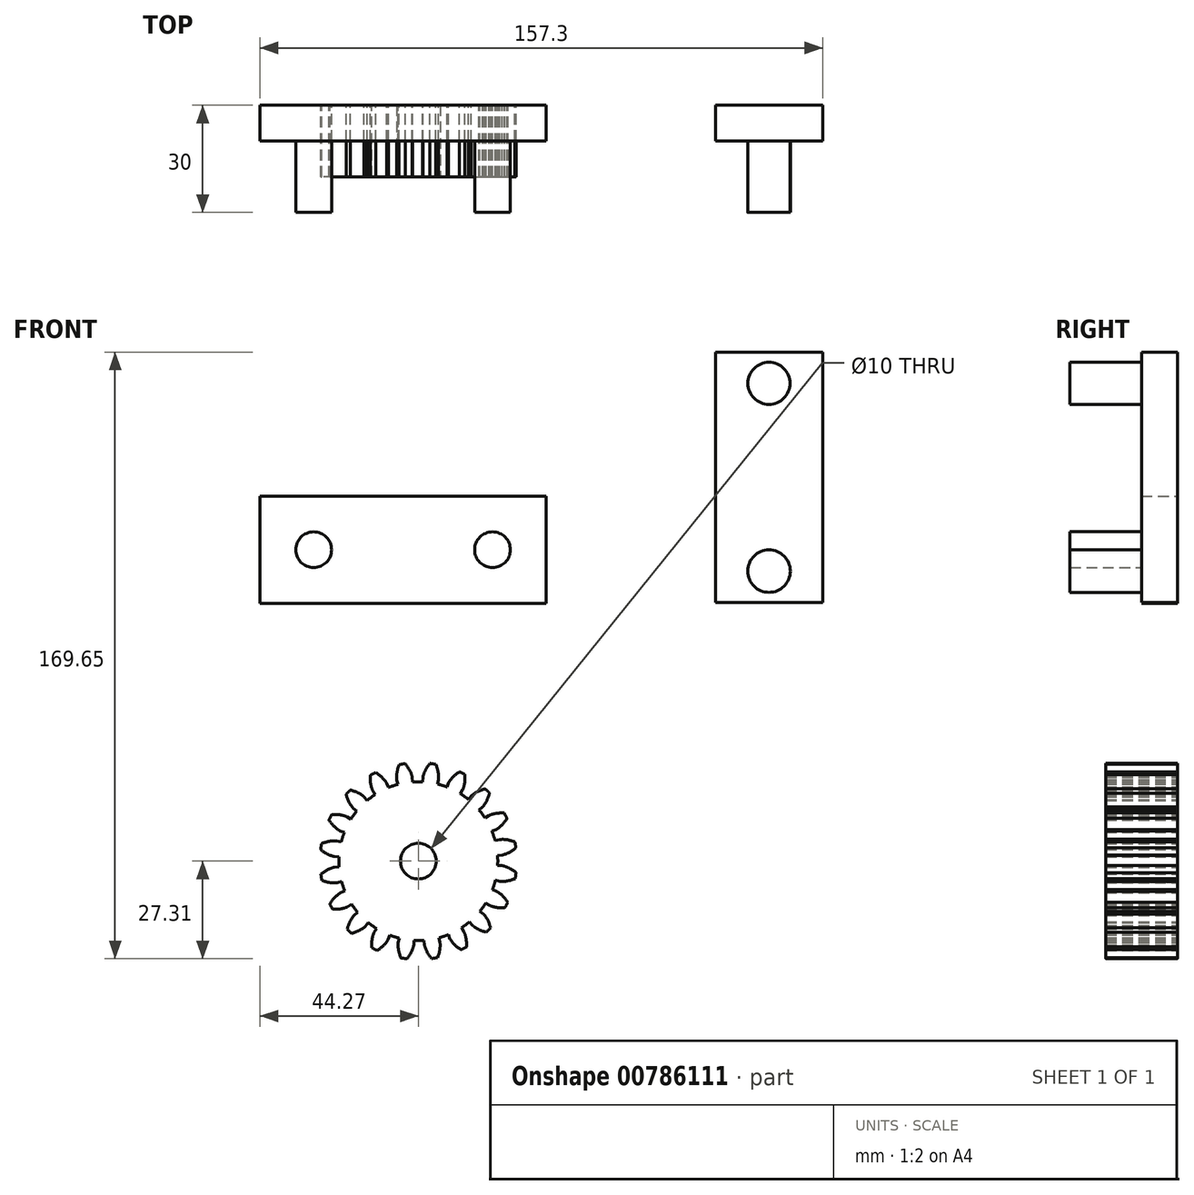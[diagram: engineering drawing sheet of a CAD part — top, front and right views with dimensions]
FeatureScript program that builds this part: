
annotation { "Feature Type Name" : "Feature", "Feature Type Description" : "" }
export const myFeature = defineFeature(function(context is Context, id is Id, definition is map)
    precondition{}
    {
        {
            var Q0;
            Q0=qCreatedBy(makeId("Front.planeOp"),FACE);
            var sketch = newSketch(context, id + "F0", { "sketchPlane" : qUnion([Q0])});
            skArc(sketch, "E0.0", {"start": v(-3.7, 27.25) * mm, "mid": v(-4.55, 27.12) * mm, "end": v(-5.4, 26.97) * mm});
            skFitSpline(sketch, "E1", {"points": [v(-6.03, 22.7) * mm, v(-6.06, 22.88) * mm, v(-6.08, 23.4) * mm, v(-6.05, 24.27) * mm, v(-5.85, 25.47) * mm, v(-5.4, 26.97) * mm], "startDerivative": vector(-0.34, 1.58) * mm, "endDerivative": vector(1.75, 5.4) * mm});
            skCircle(sketch, "E2", {"center": v(-120, 0) * mm, "radius": 25 * mm});
            skCircle(sketch, "E3.0", {"center": v(-120, 0) * mm, "radius": 27.5 * mm});
            skCircle(sketch, "E4.0", {"center": v(-120, 0) * mm, "radius": 22.2 * mm});
            skLineSegment(sketch, "E5", {"start": v(-140.88, 25) * mm, "end": v(-101.92, 25) * mm, "construction": true});
            skLineSegment(sketch, "E6", {"start": v(-111.97, 22.08) * mm, "end": v(-125.4, 26.97) * mm});
            skArc(sketch, "E7", {"start": v(-111.97, 22.08) * mm, "mid": v(-118.95, 23.47) * mm, "end": v(-126.03, 22.7) * mm});
            skLineSegment(sketch, "E8", {"start": v(-125.4, 26.97) * mm, "end": v(-120, 0) * mm});
            skLineSegment(sketch, "E9", {"start": v(-111.97, 22.08) * mm, "end": v(-120, 0) * mm});
            skLineSegment(sketch, "E10", {"start": v(-126.03, 22.7) * mm, "end": v(-120, 0) * mm});
            skPoint(sketch, "E11", {"position": v(-111.97, 22.08) * mm});
            skPoint(sketch, "E12", {"position": v(-114.7, 22.89) * mm});
            skPoint(sketch, "E13", {"position": v(-117.52, 23.36) * mm});
            skPoint(sketch, "E14", {"position": v(-120.36, 22.2) * mm});
            skPoint(sketch, "E15", {"position": v(-123.23, 23.27) * mm});
            skLineSegment(sketch, "E16", {"start": v(-117.52, 23.36) * mm, "end": v(-120, 0) * mm});
            skLineSegment(sketch, "E17", {"start": v(-120.36, 22.2) * mm, "end": v(-120, 0) * mm});
            skLineSegment(sketch, "E18", {"start": v(-123.23, 23.27) * mm, "end": v(-120, 0) * mm});
            skLineSegment(sketch, "E19", {"start": v(-114.7, 22.89) * mm, "end": v(-120, 0) * mm});
            skLineSegment(sketch, "E20", {"start": v(-120.36, 22.2) * mm, "end": v(-120.36, 23.49) * mm});
            skLineSegment(sketch, "E21", {"start": v(-114.7, 22.89) * mm, "end": v(-125.85, 25.47) * mm});
            skLineSegment(sketch, "E22", {"start": v(-117.52, 23.36) * mm, "end": v(-126.05, 24.27) * mm});
            skLineSegment(sketch, "E23", {"start": v(-120.36, 23.49) * mm, "end": v(-126.08, 23.4) * mm});
            skLineSegment(sketch, "E24", {"start": v(-123.23, 23.27) * mm, "end": v(-126.06, 22.88) * mm});
            skFitSpline(sketch, "E25", {"points": [v(-126.03, 22.7) * mm, v(-126.06, 22.88) * mm, v(-126.08, 23.4) * mm, v(-126.05, 24.27) * mm, v(-125.85, 25.47) * mm, v(-125.4, 26.97) * mm], "startDerivative": vector(-0.34, 1.58) * mm, "endDerivative": vector(1.75, 5.4) * mm});
            skFitSpline(sketch, "E26.MirrorCS", {"points": [v(-1.7, 23.43) * mm, v(-1.73, 23.6) * mm, v(-1.89, 24.1) * mm, v(-2.19, 24.91) * mm, v(-2.78, 25.98) * mm, v(-3.7, 27.25) * mm], "startDerivative": vector(-0.2, 1.6) * mm, "endDerivative": vector(-3.42, 4.53) * mm});
            skLineSegment(sketch, "E27.MirrorCS", {"start": v(-1.7, 23.43) * mm, "end": v(-1.6, 22.14) * mm});
            skCircle(sketch, "E28", {"center": v(101.91, -1.04) * mm, "radius": 25 * mm});
            skCircle(sketch, "E29.0", {"center": v(101.91, -1.04) * mm, "radius": 27.5 * mm});
            skCircle(sketch, "E30.0", {"center": v(101.91, -1.04) * mm, "radius": 22.2 * mm});
            skLineSegment(sketch, "E31", {"start": v(95.88, 21.66) * mm, "end": v(101.91, -1.04) * mm});
            skFitSpline(sketch, "E32", {"points": [v(95.88, 21.66) * mm, v(95.85, 21.84) * mm, v(95.84, 22.36) * mm, v(95.86, 23.23) * mm, v(96.07, 24.43) * mm, v(96.52, 25.93) * mm], "startDerivative": vector(-0.34, 1.58) * mm, "endDerivative": vector(1.75, 5.4) * mm});
            skLineSegment(sketch, "E33", {"start": v(101.91, -1.04) * mm, "end": v(95.86, 23.22) * mm});
            skLineSegment(sketch, "E34.1.0", {"start": v(101.91, -1.02) * mm, "end": v(92.14, 21.99) * mm});
            skLineSegment(sketch, "E34.2.0", {"start": v(101.9, -1) * mm, "end": v(88.65, 20.2) * mm});
            skLineSegment(sketch, "E34.3.0", {"start": v(101.9, -0.99) * mm, "end": v(85.49, 17.87) * mm});
            skLineSegment(sketch, "E34.4.0", {"start": v(101.88, -0.98) * mm, "end": v(82.73, 15.09) * mm});
            skLineSegment(sketch, "E34.5.0", {"start": v(101.87, -0.96) * mm, "end": v(80.43, 11.9) * mm});
            skLineSegment(sketch, "E34.6.0", {"start": v(101.85, -0.95) * mm, "end": v(78.67, 8.4) * mm});
            skLineSegment(sketch, "E34.7.0", {"start": v(101.83, -0.95) * mm, "end": v(77.47, 4.67) * mm});
            skLineSegment(sketch, "E34.8.0", {"start": v(101.82, -0.94) * mm, "end": v(76.88, 0.8) * mm});
            skLineSegment(sketch, "E34.9.0", {"start": v(101.8, -0.94) * mm, "end": v(76.9, -3.13) * mm});
            skLineSegment(sketch, "E34.10.0", {"start": v(101.78, -0.94) * mm, "end": v(77.52, -7) * mm});
            skLineSegment(sketch, "E34.11.0", {"start": v(101.76, -0.95) * mm, "end": v(78.75, -10.72) * mm});
            skLineSegment(sketch, "E34.12.0", {"start": v(101.74, -0.95) * mm, "end": v(80.55, -14.2) * mm});
            skLineSegment(sketch, "E34.13.0", {"start": v(101.73, -0.96) * mm, "end": v(82.86, -17.37) * mm});
            skLineSegment(sketch, "E34.14.0", {"start": v(101.71, -0.98) * mm, "end": v(85.65, -20.13) * mm});
            skLineSegment(sketch, "E34.15.0", {"start": v(101.7, -1) * mm, "end": v(88.83, -22.42) * mm});
            skLineSegment(sketch, "E34.16.0", {"start": v(101.7, -1) * mm, "end": v(92.33, -24.19) * mm});
            skLineSegment(sketch, "E34.17.0", {"start": v(101.69, -1.02) * mm, "end": v(96.07, -25.38) * mm});
            skLineSegment(sketch, "E34.18.0", {"start": v(101.68, -1.04) * mm, "end": v(99.94, -25.98) * mm});
            skLineSegment(sketch, "E34.19.0", {"start": v(101.68, -1.06) * mm, "end": v(103.87, -25.96) * mm});
            skLineSegment(sketch, "E34.20.0", {"start": v(101.68, -1.08) * mm, "end": v(107.74, -25.33) * mm});
            skLineSegment(sketch, "E34.21.0", {"start": v(101.69, -1.1) * mm, "end": v(111.46, -24.1) * mm});
            skLineSegment(sketch, "E34.22.0", {"start": v(101.7, -1.11) * mm, "end": v(114.95, -22.31) * mm});
            skLineSegment(sketch, "E34.23.0", {"start": v(101.7, -1.13) * mm, "end": v(118.1, -20) * mm});
            skLineSegment(sketch, "E34.24.0", {"start": v(101.72, -1.14) * mm, "end": v(120.87, -17.2) * mm});
            skLineSegment(sketch, "E34.25.0", {"start": v(101.73, -1.16) * mm, "end": v(123.16, -14.03) * mm});
            skLineSegment(sketch, "E34.26.0", {"start": v(101.75, -1.17) * mm, "end": v(124.93, -10.52) * mm});
            skLineSegment(sketch, "E34.27.0", {"start": v(101.76, -1.17) * mm, "end": v(126.12, -6.79) * mm});
            skLineSegment(sketch, "E34.28.0", {"start": v(101.78, -1.18) * mm, "end": v(126.72, -2.91) * mm});
            skLineSegment(sketch, "E34.29.0", {"start": v(101.8, -1.18) * mm, "end": v(126.7, 1) * mm});
            skLineSegment(sketch, "E34.30.0", {"start": v(101.82, -1.18) * mm, "end": v(126.07, 4.88) * mm});
            skLineSegment(sketch, "E34.31.0", {"start": v(101.84, -1.17) * mm, "end": v(124.85, 8.6) * mm});
            skLineSegment(sketch, "E34.32.0", {"start": v(101.85, -1.16) * mm, "end": v(123.05, 12.09) * mm});
            skLineSegment(sketch, "E34.33.0", {"start": v(101.87, -1.15) * mm, "end": v(120.73, 15.25) * mm});
            skLineSegment(sketch, "E34.34.0", {"start": v(101.88, -1.14) * mm, "end": v(117.95, 18.01) * mm});
            skLineSegment(sketch, "E34.35.0", {"start": v(101.9, -1.13) * mm, "end": v(114.76, 20.3) * mm});
            skLineSegment(sketch, "E34.36.0", {"start": v(101.9, -1.11) * mm, "end": v(111.26, 22.07) * mm});
            skLineSegment(sketch, "E34.37.0", {"start": v(101.91, -1.1) * mm, "end": v(107.53, 23.27) * mm});
            skLineSegment(sketch, "E34.38.0", {"start": v(101.92, -1.08) * mm, "end": v(103.65, 23.86) * mm});
            skLineSegment(sketch, "E34.39.0", {"start": v(101.92, -1.06) * mm, "end": v(99.73, 23.85) * mm});
            skPoint(sketch, "E34.center", {"position": v(101.8, -1.06) * mm});
            skLineSegment(sketch, "E35", {"start": v(101.91, -1.04) * mm, "end": v(96.33, 32.27) * mm});
            skFitSpline(sketch, "E36.MirrorCS", {"points": [v(100.21, 22.4) * mm, v(100.19, 22.56) * mm, v(100.03, 23.06) * mm, v(99.72, 23.87) * mm, v(99.14, 24.94) * mm, v(98.22, 26.21) * mm], "startDerivative": vector(-0.2, 1.6) * mm, "endDerivative": vector(-3.42, 4.53) * mm});
            skLineSegment(sketch, "E37.MirrorCS", {"start": v(100.21, 22.4) * mm, "end": v(101.91, -1.04) * mm});
            skLineSegment(sketch, "E38", {"start": v(101.91, -1.04) * mm, "end": v(91.07, 29.73) * mm});
            skLineSegment(sketch, "E39.MirrorCS", {"start": v(101.91, -1.04) * mm, "end": v(102.13, 31.59) * mm});
            skLineSegment(sketch, "E40", {"start": v(-6.03, 22.7) * mm, "end": v(-5.7, 21.46) * mm});
            skArc(sketch, "E41", {"start": v(-1.6, 22.14) * mm, "mid": v(-3.67, 21.9) * mm, "end": v(-5.7, 21.46) * mm});
            skSolve(sketch);
        }
        {
            var Q0;
            Q0=makeQuery(id+"F0.imprint","IMPRINT",FACE,{"disambiguationData":[TD([[makeQuery(id+"F0.imprint","IMPRINT",EDGE,{"derivedFrom":sQuery(id+"F0.wireOp",EDGE,"E0.0")}),1.0]])]});
            extrude(context, id + "F1", {"entities" : qUnion([Q0]), "depth" : 20 * mm, "offsetDistance" : 25 * mm});
        }
        {
            var Q0;
            Q0=qCreatedBy(makeId("Top.planeOp"),FACE);
            var sketch = newSketch(context, id + "F2", { "sketchPlane" : qUnion([Q0])});
            skLineSegment(sketch, "E42", {"start": v(0, -28.63) * mm, "end": v(0, 36.77) * mm, "construction": true});
            skSolve(sketch);
        }
        {
            var Q0;
            Q0=makeQuery(id+"F1.opExtrude","SWEPT_BODY",BODY,{"disambiguationData":[OSD([sQuery(id+"F0.wireOp",EDGE,"E0.0"),sQuery(id+"F0.wireOp",EDGE,"E1"),sQuery(id+"F0.wireOp",EDGE,"E26.MirrorCS"),sQuery(id+"F0.wireOp",EDGE,"E27.MirrorCS"),sQuery(id+"F0.wireOp",EDGE,"E40"),sQuery(id+"F0.wireOp",EDGE,"E41")])]});
            var Q1;
            Q1=sQuery(id+"F2.wireOp",EDGE,"E42");
            circularPattern(context, id + "F3", {"entities" : qUnion([Q0]), "axis" : qUnion([Q1]), "angle" : 360 * degree, "instanceCount" : 20, "equalSpace" : true});
        }
        {
            var Q0;
            Q0=qCreatedBy(makeId("Front.planeOp"),FACE);
            var sketch = newSketch(context, id + "F4", { "sketchPlane" : qUnion([Q0])});
            skArc(sketch, "E43", {"start": v(-4.6, 21.72) * mm, "mid": v(3.61, -21.9) * mm, "end": v(-2.62, 22.05) * mm});
            skLineSegment(sketch, "E44", {"start": v(-2.62, 22.05) * mm, "end": v(-3.88, 23.51) * mm});
            skLineSegment(sketch, "E45", {"start": v(-3.88, 23.51) * mm, "end": v(-4.6, 21.72) * mm});
            skLineSegment(sketch, "E46.1.0", {"start": v(-9.3, 20.16) * mm, "end": v(-10.95, 21.16) * mm});
            skLineSegment(sketch, "E46.1.1", {"start": v(-10.95, 21.16) * mm, "end": v(-11.09, 19.23) * mm});
            skLineSegment(sketch, "E46.2.0", {"start": v(-15.08, 16.3) * mm, "end": v(-16.96, 16.74) * mm});
            skLineSegment(sketch, "E46.2.1", {"start": v(-16.96, 16.74) * mm, "end": v(-16.49, 14.87) * mm});
            skLineSegment(sketch, "E46.3.0", {"start": v(-19.37, 10.84) * mm, "end": v(-21.3, 10.68) * mm});
            skLineSegment(sketch, "E46.3.1", {"start": v(-21.3, 10.68) * mm, "end": v(-20.27, 9.04) * mm});
            skLineSegment(sketch, "E46.4.0", {"start": v(-21.78, 4.32) * mm, "end": v(-23.56, 3.58) * mm});
            skLineSegment(sketch, "E46.4.1", {"start": v(-23.56, 3.58) * mm, "end": v(-22.08, 2.34) * mm});
            skLineSegment(sketch, "E46.5.0", {"start": v(-22.05, -2.62) * mm, "end": v(-23.51, -3.88) * mm});
            skLineSegment(sketch, "E46.5.1", {"start": v(-23.51, -3.88) * mm, "end": v(-21.72, -4.6) * mm});
            skLineSegment(sketch, "E46.6.0", {"start": v(-20.16, -9.3) * mm, "end": v(-21.16, -10.95) * mm});
            skLineSegment(sketch, "E46.6.1", {"start": v(-21.16, -10.95) * mm, "end": v(-19.23, -11.09) * mm});
            skLineSegment(sketch, "E46.7.0", {"start": v(-16.3, -15.08) * mm, "end": v(-16.74, -16.96) * mm});
            skLineSegment(sketch, "E46.7.1", {"start": v(-16.74, -16.96) * mm, "end": v(-14.87, -16.49) * mm});
            skLineSegment(sketch, "E46.8.0", {"start": v(-10.84, -19.37) * mm, "end": v(-10.68, -21.3) * mm});
            skLineSegment(sketch, "E46.8.1", {"start": v(-10.68, -21.3) * mm, "end": v(-9.04, -20.27) * mm});
            skLineSegment(sketch, "E46.9.0", {"start": v(-4.32, -21.78) * mm, "end": v(-3.58, -23.56) * mm});
            skLineSegment(sketch, "E46.9.1", {"start": v(-3.58, -23.56) * mm, "end": v(-2.34, -22.08) * mm});
            skLineSegment(sketch, "E46.10.0", {"start": v(2.62, -22.05) * mm, "end": v(3.88, -23.51) * mm});
            skLineSegment(sketch, "E46.10.1", {"start": v(3.88, -23.51) * mm, "end": v(4.6, -21.72) * mm});
            skLineSegment(sketch, "E46.11.0", {"start": v(9.3, -20.16) * mm, "end": v(10.95, -21.16) * mm});
            skLineSegment(sketch, "E46.11.1", {"start": v(10.95, -21.16) * mm, "end": v(11.09, -19.23) * mm});
            skLineSegment(sketch, "E46.12.0", {"start": v(15.08, -16.3) * mm, "end": v(16.96, -16.74) * mm});
            skLineSegment(sketch, "E46.12.1", {"start": v(16.96, -16.74) * mm, "end": v(16.49, -14.87) * mm});
            skLineSegment(sketch, "E46.13.0", {"start": v(19.37, -10.84) * mm, "end": v(21.3, -10.68) * mm});
            skLineSegment(sketch, "E46.13.1", {"start": v(21.3, -10.68) * mm, "end": v(20.27, -9.04) * mm});
            skLineSegment(sketch, "E46.14.0", {"start": v(21.78, -4.32) * mm, "end": v(23.56, -3.58) * mm});
            skLineSegment(sketch, "E46.14.1", {"start": v(23.56, -3.58) * mm, "end": v(22.08, -2.34) * mm});
            skLineSegment(sketch, "E46.15.0", {"start": v(22.05, 2.62) * mm, "end": v(23.51, 3.88) * mm});
            skLineSegment(sketch, "E46.15.1", {"start": v(23.51, 3.88) * mm, "end": v(21.72, 4.6) * mm});
            skLineSegment(sketch, "E46.16.0", {"start": v(20.16, 9.3) * mm, "end": v(21.16, 10.95) * mm});
            skLineSegment(sketch, "E46.16.1", {"start": v(21.16, 10.95) * mm, "end": v(19.23, 11.09) * mm});
            skLineSegment(sketch, "E46.17.0", {"start": v(16.3, 15.08) * mm, "end": v(16.74, 16.96) * mm});
            skLineSegment(sketch, "E46.17.1", {"start": v(16.74, 16.96) * mm, "end": v(14.87, 16.49) * mm});
            skLineSegment(sketch, "E46.18.0", {"start": v(10.84, 19.37) * mm, "end": v(10.68, 21.3) * mm});
            skLineSegment(sketch, "E46.18.1", {"start": v(10.68, 21.3) * mm, "end": v(9.04, 20.27) * mm});
            skLineSegment(sketch, "E46.19.0", {"start": v(4.32, 21.78) * mm, "end": v(3.58, 23.56) * mm});
            skLineSegment(sketch, "E46.19.1", {"start": v(3.58, 23.56) * mm, "end": v(2.34, 22.08) * mm});
            skCircle(sketch, "E47", {"center": v(0, 0) * mm, "radius": 5 * mm});
            skSolve(sketch);
        }
        {
            var Q0;
            Q0=makeQuery(id+"F4.imprint","IMPRINT",FACE,{"disambiguationData":[TD([[makeQuery(id+"F4.imprint","IMPRINT",EDGE,{"derivedFrom":sQuery(id+"F4.wireOp",EDGE,"E43")}),1.0]])]});
            extrude(context, id + "F5", {"entities" : qUnion([Q0]), "operationType" : NewBodyOperationType.ADD, "depth" : 20 * mm, "offsetDistance" : 25 * mm});
        }
        {
            var Q0;
            Q0=qCreatedBy(makeId("Front.planeOp"),FACE);
            var sketch = newSketch(context, id + "F6", { "sketchPlane" : qUnion([Q0])});
            skLineSegment(sketch, "E48.bottom", {"start": v(-44.27, 102.06) * mm, "end": v(35.73, 102.06) * mm});
            skLineSegment(sketch, "E48.top", {"start": v(-44.27, 72.06) * mm, "end": v(35.73, 72.06) * mm});
            skLineSegment(sketch, "E48.left", {"start": v(-44.27, 102.06) * mm, "end": v(-44.27, 72.06) * mm});
            skLineSegment(sketch, "E48.right", {"start": v(35.73, 102.06) * mm, "end": v(35.73, 72.06) * mm});
            skCircle(sketch, "E49", {"center": v(-29.27, 87.06) * mm, "radius": 5 * mm});
            skCircle(sketch, "E50", {"center": v(20.73, 87.06) * mm, "radius": 5 * mm});
            skLineSegment(sketch, "E51", {"start": v(-29.27, 87.06) * mm, "end": v(20.73, 87.06) * mm, "construction": true});
            skSolve(sketch);
        }
        {
            var Q0;
            Q0 = qSketchRegion(id + "F6", true);
            var Q1;
            Q1=makeQuery(id+"F6.imprint","IMPRINT",FACE,{"disambiguationData":[TD([[makeQuery(id+"F6.imprint","IMPRINT",EDGE,{"derivedFrom":sQuery(id+"F6.wireOp",EDGE,"E49")}),1.0]])]});
            var Q2;
            Q2=makeQuery(id+"F6.imprint","IMPRINT",FACE,{"disambiguationData":[TD([[makeQuery(id+"F6.imprint","IMPRINT",EDGE,{"derivedFrom":sQuery(id+"F6.wireOp",EDGE,"E50")}),1.0]])]});
            extrude(context, id + "F7", {"entities" : qUnion([Q0, Q1, Q2]), "depth" : 10 * mm, "offsetDistance" : 25 * mm});
        }
        {
            var Q0;
            Q0=makeQuery(id+"F6.imprint","IMPRINT",FACE,{"disambiguationData":[TD([[makeQuery(id+"F6.imprint","IMPRINT",EDGE,{"derivedFrom":sQuery(id+"F6.wireOp",EDGE,"E49")}),1.0]])]});
            var Q1;
            Q1=makeQuery(id+"F6.imprint","IMPRINT",FACE,{"disambiguationData":[TD([[makeQuery(id+"F6.imprint","IMPRINT",EDGE,{"derivedFrom":sQuery(id+"F6.wireOp",EDGE,"E50")}),1.0]])]});
            extrude(context, id + "F8", {"entities" : qUnion([Q0, Q1]), "operationType" : NewBodyOperationType.ADD, "depth" : 30 * mm, "offsetDistance" : 25 * mm});
        }
        {
            var Q0;
            Q0=qCreatedBy(makeId("Front.planeOp"),FACE);
            var sketch = newSketch(context, id + "F9", { "sketchPlane" : qUnion([Q0])});
            skLineSegment(sketch, "E52.bottom", {"start": v(83.03, 142.34) * mm, "end": v(113.03, 142.34) * mm});
            skLineSegment(sketch, "E52.top", {"start": v(83.03, 72.34) * mm, "end": v(113.03, 72.34) * mm});
            skLineSegment(sketch, "E52.left", {"start": v(83.03, 142.34) * mm, "end": v(83.03, 72.34) * mm});
            skLineSegment(sketch, "E52.right", {"start": v(113.03, 142.34) * mm, "end": v(113.03, 72.34) * mm});
            skCircle(sketch, "E53", {"center": v(98.03, 133.59) * mm, "radius": 5.9 * mm});
            skCircle(sketch, "E54", {"center": v(98.03, 81.09) * mm, "radius": 5.95 * mm});
            skLineSegment(sketch, "E55", {"start": v(98.03, 133.59) * mm, "end": v(98.03, 81.09) * mm, "construction": true});
            skSolve(sketch);
        }
        {
            var Q0;
            Q0=makeQuery(id+"F9.imprint","IMPRINT",FACE,{"disambiguationData":[TD([[makeQuery(id+"F9.imprint","IMPRINT",EDGE,{"derivedFrom":sQuery(id+"F9.wireOp",EDGE,"E52.bottom")}),-1.0]])]});
            extrude(context, id + "F10", {"entities" : qUnion([Q0]), "depth" : 10 * mm, "offsetDistance" : 25 * mm});
        }
        {
            var Q0;
            Q0=makeQuery(id+"F9.imprint","IMPRINT",FACE,{"disambiguationData":[TD([[makeQuery(id+"F9.imprint","IMPRINT",EDGE,{"derivedFrom":sQuery(id+"F9.wireOp",EDGE,"E53")}),1.0]])]});
            var Q1;
            Q1=makeQuery(id+"F9.imprint","IMPRINT",FACE,{"disambiguationData":[TD([[makeQuery(id+"F9.imprint","IMPRINT",EDGE,{"derivedFrom":sQuery(id+"F9.wireOp",EDGE,"E54")}),1.0]])]});
            extrude(context, id + "F11", {"entities" : qUnion([Q0, Q1]), "operationType" : NewBodyOperationType.ADD, "depth" : 30 * mm, "offsetDistance" : 25 * mm});
        }
    });
